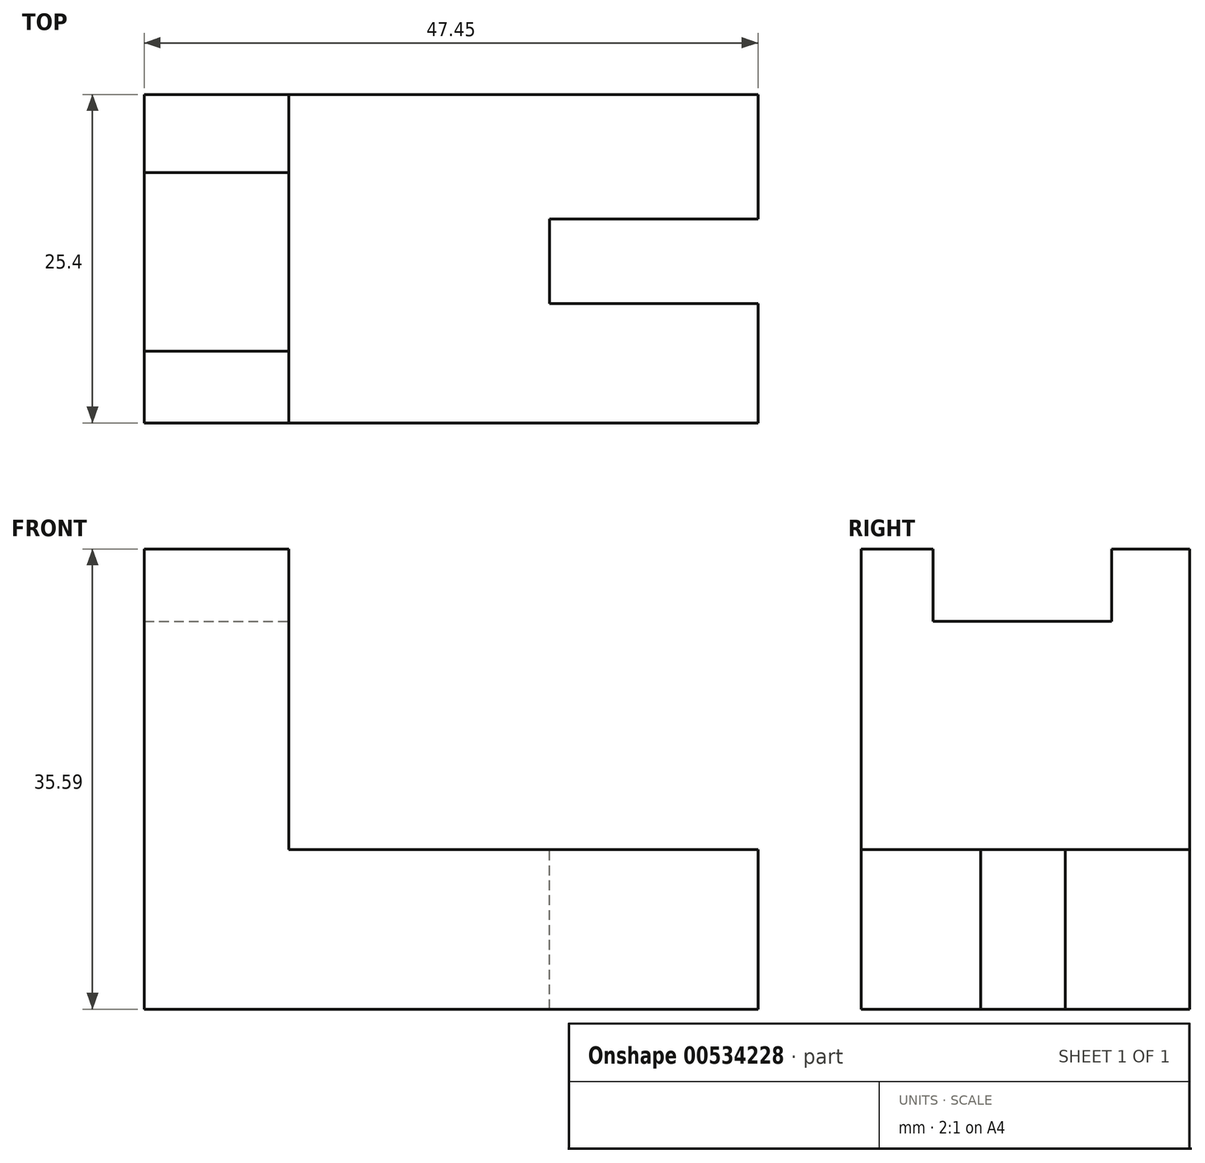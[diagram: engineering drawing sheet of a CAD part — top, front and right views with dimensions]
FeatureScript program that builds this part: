
annotation { "Feature Type Name" : "Feature", "Feature Type Description" : "" }
export const myFeature = defineFeature(function(context is Context, id is Id, definition is map)
    precondition{}
    {
        {
            var Q0;
            Q0=qCreatedBy(makeId("Front.planeOp"),FACE);
            var sketch = newSketch(context, id + "F0", { "sketchPlane" : qUnion([Q0])});
            skLineSegment(sketch, "E0", {"start": v(0, 0) * mm, "end": v(-47.45, 0) * mm});
            skLineSegment(sketch, "E1", {"start": v(-47.45, 0) * mm, "end": v(-47.45, 35.59) * mm});
            skLineSegment(sketch, "E2", {"start": v(-47.45, 35.59) * mm, "end": v(-36.28, 35.59) * mm});
            skLineSegment(sketch, "E3", {"start": v(-36.28, 35.59) * mm, "end": v(-36.28, 12.33) * mm});
            skLineSegment(sketch, "E4", {"start": v(-36.28, 12.33) * mm, "end": v(0, 12.33) * mm});
            skLineSegment(sketch, "E5", {"start": v(0, 12.33) * mm, "end": v(0, 0) * mm});
            skSolve(sketch);
        }
        {
            var Q0;
            Q0=makeQuery(id+"F0.imprint","IMPRINT",FACE,{"disambiguationData":[TD([[makeQuery(id+"F0.imprint","IMPRINT",EDGE,{"derivedFrom":sQuery(id+"F0.wireOp",EDGE,"E0")}),-1.0]])]});
            extrude(context, id + "F1", {"entities" : qUnion([Q0]), "depth" : 25.4 * mm, "offsetDistance" : 25.4 * mm});
        }
        {
            var Q0;
            Q0=makeQuery(id+"F1.opExtrude","SWEPT_FACE",FACE,{"disambiguationData":[OSD([sQuery(id+"F0.wireOp",EDGE,"E3")])]});
            var sketch = newSketch(context, id + "F2", { "sketchPlane" : qUnion([Q0])});
            skLineSegment(sketch, "E6.bottom", {"start": v(-19.86, 35.59) * mm, "end": v(-6.05, 35.59) * mm});
            skLineSegment(sketch, "E6.top", {"start": v(-19.86, 29.98) * mm, "end": v(-6.05, 29.98) * mm});
            skLineSegment(sketch, "E6.left", {"start": v(-19.86, 35.59) * mm, "end": v(-19.86, 29.98) * mm});
            skLineSegment(sketch, "E6.right", {"start": v(-6.05, 35.59) * mm, "end": v(-6.05, 29.98) * mm});
            skSolve(sketch);
        }
        {
            var Q0;
            Q0=makeQuery(id+"F2.imprint","IMPRINT",FACE,{"disambiguationData":[TD([[makeQuery(id+"F2.imprint","IMPRINT",EDGE,{"derivedFrom":sQuery(id+"F2.wireOp",EDGE,"E6.bottom")}),-1.0]])]});
            extrude(context, id + "F3", {"entities" : qUnion([Q0]), "operationType" : NewBodyOperationType.REMOVE, "oppositeDirection" : true, "depth" : 25.4 * mm, "offsetDistance" : 25.4 * mm});
        }
        {
            var Q0;
            Q0=makeQuery(id+"F1.opExtrude","SWEPT_FACE",FACE,{"disambiguationData":[OSD([sQuery(id+"F0.wireOp",EDGE,"E4")])]});
            var sketch = newSketch(context, id + "F4", { "sketchPlane" : qUnion([Q0])});
            skLineSegment(sketch, "E7.bottom", {"start": v(0, -9.62) * mm, "end": v(-16.12, -9.62) * mm});
            skLineSegment(sketch, "E7.top", {"start": v(0, -16.18) * mm, "end": v(-16.12, -16.18) * mm});
            skLineSegment(sketch, "E7.left", {"start": v(0, -9.62) * mm, "end": v(0, -16.18) * mm});
            skLineSegment(sketch, "E7.right", {"start": v(-16.12, -9.62) * mm, "end": v(-16.12, -16.18) * mm});
            skSolve(sketch);
        }
        {
            var Q0;
            Q0=makeQuery(id+"F4.imprint","IMPRINT",FACE,{"disambiguationData":[TD([[makeQuery(id+"F4.imprint","IMPRINT",EDGE,{"derivedFrom":sQuery(id+"F4.wireOp",EDGE,"E7.bottom")}),1.0]])]});
            extrude(context, id + "F5", {"entities" : qUnion([Q0]), "operationType" : NewBodyOperationType.REMOVE, "oppositeDirection" : true, "depth" : 25.4 * mm, "offsetDistance" : 25.4 * mm});
        }
    });
